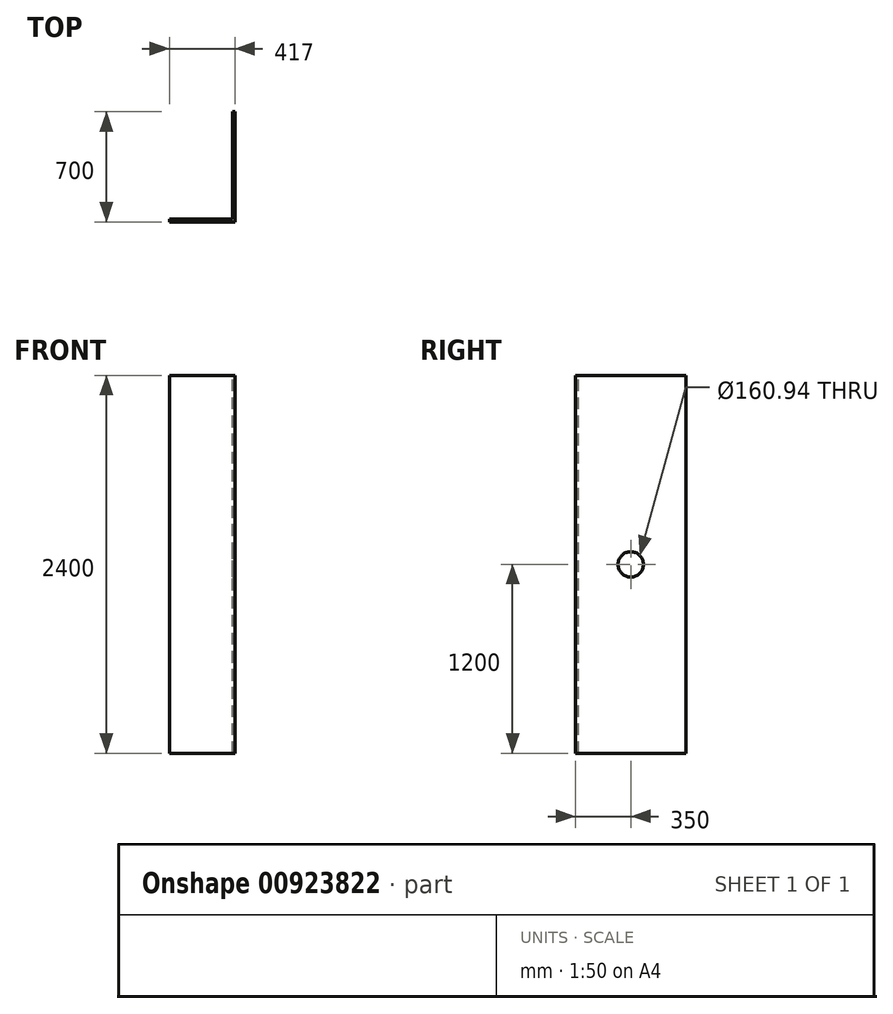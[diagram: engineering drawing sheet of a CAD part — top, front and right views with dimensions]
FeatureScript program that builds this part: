
annotation { "Feature Type Name" : "Feature", "Feature Type Description" : "" }
export const myFeature = defineFeature(function(context is Context, id is Id, definition is map)
    precondition{}
    {
        {
            var Q0;
            Q0=qCreatedBy(makeId("Front.planeOp"),FACE);
            var sketch = newSketch(context, id + "F0", { "sketchPlane" : qUnion([Q0])});
            skLineSegment(sketch, "E0.bottom", {"start": v(-304.64, -418.38) * mm, "end": v(95.36, -418.38) * mm});
            skLineSegment(sketch, "E0.top", {"start": v(-304.64, 1981.62) * mm, "end": v(95.36, 1981.62) * mm});
            skLineSegment(sketch, "E0.left", {"start": v(-304.64, -418.38) * mm, "end": v(-304.64, 1981.62) * mm});
            skLineSegment(sketch, "E0.right", {"start": v(95.36, -418.38) * mm, "end": v(95.36, 1981.62) * mm});
            skSolve(sketch);
        }
        {
            var Q0;
            Q0 = qSketchRegion(id + "F0", true);
            extrude(context, id + "F1", {"entities" : qUnion([Q0]), "depth" : 17 * mm, "offsetDistance" : 25 * mm});
        }
        {
            var Q0;
            Q0=makeQuery(id+"F1.opExtrude","SWEPT_FACE",FACE,{"disambiguationData":[OSD([sQuery(id+"F0.wireOp",EDGE,"E0.right")])]});
            var sketch = newSketch(context, id + "F2", { "sketchPlane" : qUnion([Q0])});
            skLineSegment(sketch, "E1.bottom", {"start": v(-17, 1981.62) * mm, "end": v(683, 1981.62) * mm});
            skLineSegment(sketch, "E1.top", {"start": v(-17, -418.38) * mm, "end": v(683, -418.38) * mm});
            skLineSegment(sketch, "E1.left", {"start": v(-17, 1981.62) * mm, "end": v(-17, -418.38) * mm});
            skLineSegment(sketch, "E1.right", {"start": v(683, 1981.62) * mm, "end": v(683, -418.38) * mm});
            skSolve(sketch);
        }
        {
            var Q0;
            Q0 = qSketchRegion(id + "F2", true);
            extrude(context, id + "F3", {"entities" : qUnion([Q0]), "operationType" : NewBodyOperationType.ADD, "depth" : 17 * mm, "offsetDistance" : 25 * mm});
        }
        {
            var Q0;
            Q0=makeQuery(id+"F3.opExtrude","CAP_FACE",FACE,{"disambiguationData":[OSD([sQuery(id+"F2.wireOp",EDGE,"E1.bottom"),sQuery(id+"F2.wireOp",EDGE,"E1.top"),sQuery(id+"F2.wireOp",EDGE,"E1.left"),sQuery(id+"F2.wireOp",EDGE,"E1.right")])],"isStart":false});
            var sketch = newSketch(context, id + "F4", { "sketchPlane" : qUnion([Q0])});
            skCircle(sketch, "E2", {"center": v(333, 781.62) * mm, "radius": 80.47 * mm});
            skPoint(sketch, "E2.centerSnap0", {"position": v(333, 1981.62) * mm});
            skPoint(sketch, "E2.centerSnap1", {"position": v(683, 781.62) * mm});
            skSolve(sketch);
        }
        {
            var Q0;
            Q0 = qSketchRegion(id + "F4", true);
            extrude(context, id + "F5", {"entities" : qUnion([Q0]), "operationType" : NewBodyOperationType.REMOVE, "oppositeDirection" : true, "depth" : 25 * mm, "offsetDistance" : 25 * mm});
        }
    });
